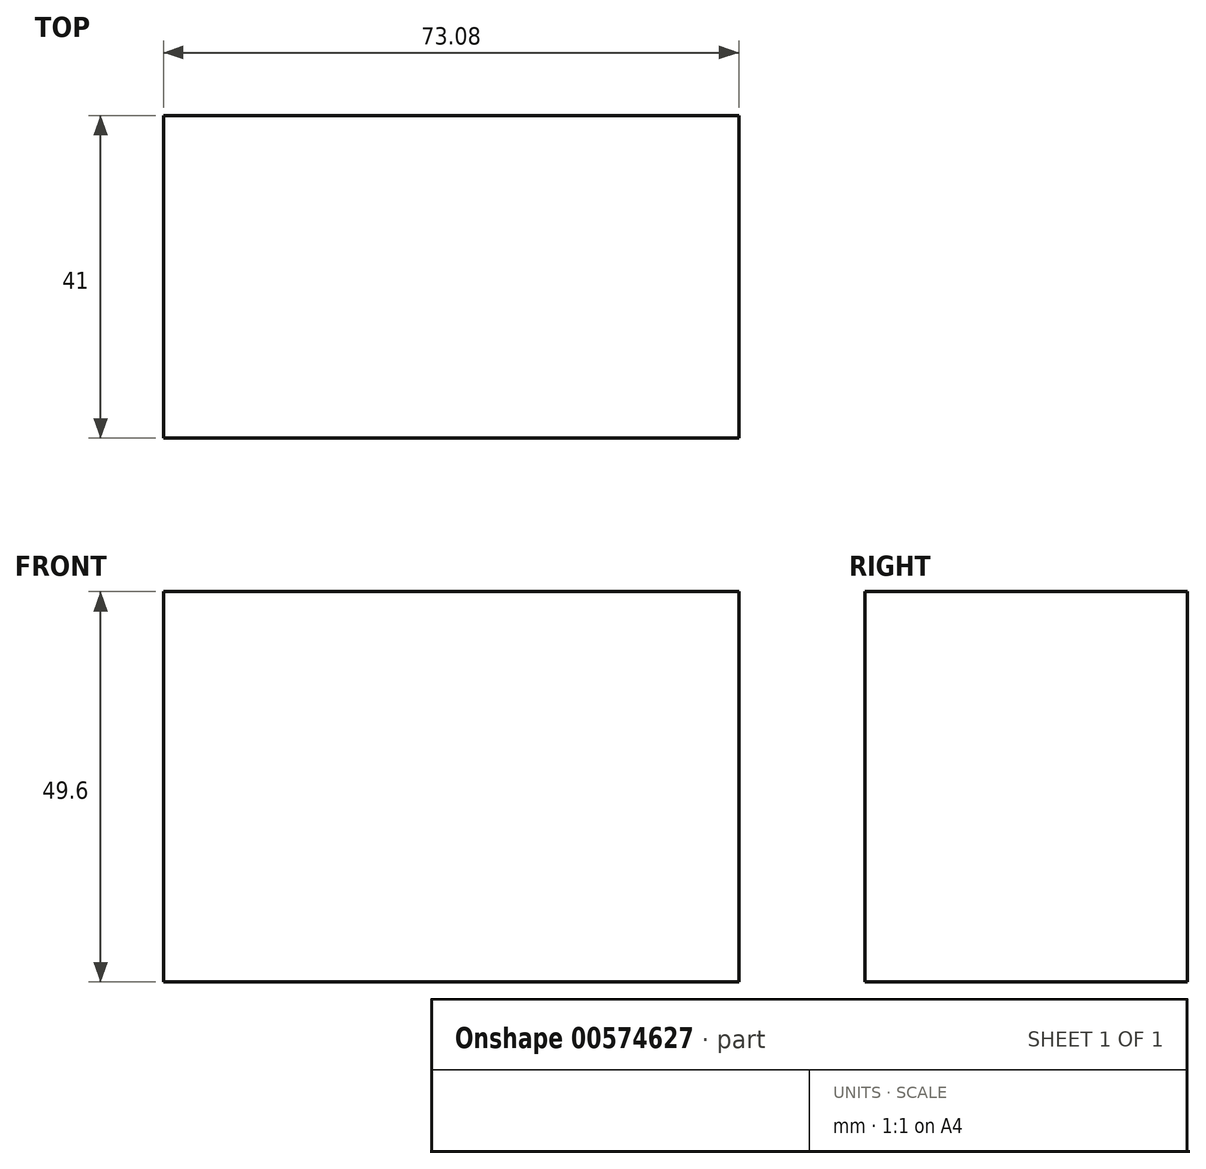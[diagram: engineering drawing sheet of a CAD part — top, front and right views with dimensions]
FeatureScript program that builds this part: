
annotation { "Feature Type Name" : "Feature", "Feature Type Description" : "" }
export const myFeature = defineFeature(function(context is Context, id is Id, definition is map)
    precondition{}
    {
        {
            var Q0;
            Q0=qCreatedBy(makeId("Front.planeOp"),FACE);
            var sketch = newSketch(context, id + "F0", { "sketchPlane" : qUnion([Q0])});
            skLineSegment(sketch, "E0.bottom", {"start": v(-36.54, 24.8) * mm, "end": v(36.54, 24.8) * mm});
            skLineSegment(sketch, "E0.top", {"start": v(-36.54, -24.8) * mm, "end": v(36.54, -24.8) * mm});
            skLineSegment(sketch, "E0.left", {"start": v(-36.54, 24.8) * mm, "end": v(-36.54, -24.8) * mm});
            skLineSegment(sketch, "E0.right", {"start": v(36.54, 24.8) * mm, "end": v(36.54, -24.8) * mm});
            skPoint(sketch, "E0.middle", {"position": v(0, 0) * mm});
            skSolve(sketch);
        }
        {
            var Q0;
            Q0=makeQuery(id+"F0.imprint","IMPRINT",FACE,{"disambiguationData":[TD([[makeQuery(id+"F0.imprint","IMPRINT",EDGE,{"derivedFrom":sQuery(id+"F0.wireOp",EDGE,"E0.bottom")}),-1.0]])]});
            extrude(context, id + "F1", {"entities" : qUnion([Q0]), "depth" : 41 * mm, "offsetDistance" : 25 * mm});
        }
    });
